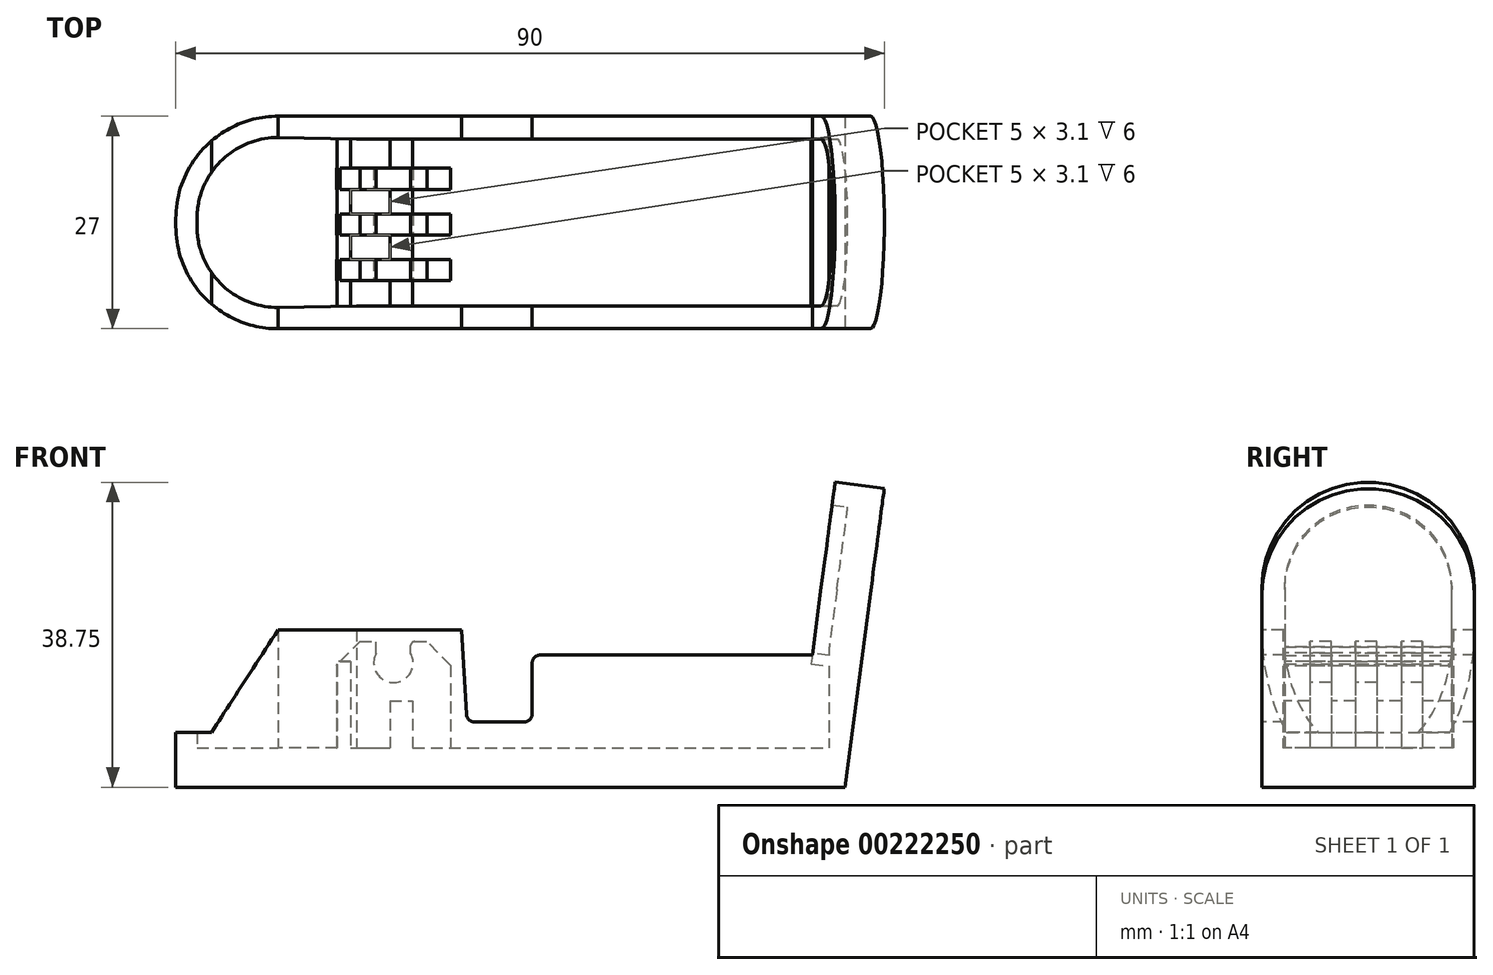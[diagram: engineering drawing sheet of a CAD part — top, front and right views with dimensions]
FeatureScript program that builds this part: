
annotation { "Feature Type Name" : "Feature", "Feature Type Description" : "" }
export const myFeature = defineFeature(function(context is Context, id is Id, definition is map)
    precondition{}
    {
        {
            var Q0;
            Q0=qCreatedBy(makeId("Top.planeOp"),FACE);
            var sketch = newSketch(context, id + "F0", { "sketchPlane" : qUnion([Q0])});
            skLineSegment(sketch, "E0.bottom", {"start": v(-17.1, 7) * mm, "end": v(54.9, 7) * mm});
            skLineSegment(sketch, "E0.top", {"start": v(-17.1, -20) * mm, "end": v(54.9, -20) * mm});
            skLineSegment(sketch, "E0.left", {"start": v(-30.1, -6) * mm, "end": v(-30.1, -7) * mm});
            skLineSegment(sketch, "E0.right", {"start": v(54.9, 7) * mm, "end": v(54.9, -20) * mm});
            skPoint(sketch, "E1.visualSharp", {"position": v(-30.1, 7) * mm});
            skArc(sketch, "E1.filletArc", {"start": v(-17.1, 7) * mm, "mid": v(-26.3, 3.19) * mm, "end": v(-30.1, -6) * mm});
            skPoint(sketch, "E2.visualSharp", {"position": v(-30.1, -20) * mm});
            skArc(sketch, "E2.filletArc", {"start": v(-30.1, -7) * mm, "mid": v(-26.3, -16.2) * mm, "end": v(-17.1, -20) * mm});
            skLineSegment(sketch, "E3.2", {"start": v(-7.15, -17.1) * mm, "end": v(52, -17.1) * mm});
            skLineSegment(sketch, "E3.3", {"start": v(-7.15, 4.1) * mm, "end": v(52.9, 4.1) * mm});
            skLineSegment(sketch, "E4", {"start": v(52.9, 7) * mm, "end": v(52.9, -20) * mm});
            skLineSegment(sketch, "E5", {"start": v(52, -17.1) * mm, "end": v(52.9, -17.1) * mm});
            skArc(sketch, "E6.0", {"start": v(-27.4, -7) * mm, "mid": v(-24.39, -14.3) * mm, "end": v(-17.1, -17.3) * mm});
            skLineSegment(sketch, "E6.1", {"start": v(-27.4, -6) * mm, "end": v(-27.4, -7) * mm});
            skArc(sketch, "E6.2", {"start": v(-17.1, 4.3) * mm, "mid": v(-24.39, 1.28) * mm, "end": v(-27.4, -6) * mm});
            skLineSegment(sketch, "E7", {"start": v(-17.1, 4.3) * mm, "end": v(-7.15, 4.1) * mm});
            skLineSegment(sketch, "E8", {"start": v(-7.15, -17.1) * mm, "end": v(-17.1, -17.3) * mm});
            skSolve(sketch);
        }
        {
            var Q0;
            Q0=makeQuery(id+"F0.imprint","IMPRINT",FACE,{"disambiguationData":[TD([[makeQuery(id+"F0.imprint","IMPRINT",EDGE,{"derivedFrom":sQuery(id+"F0.wireOp",EDGE,"E0.bottom")}),-1.0]])]});
            var Q1;
            Q1=makeQuery(id+"F0.imprint","IMPRINT",FACE,{"disambiguationData":[TD([[makeQuery(id+"F0.imprint","IMPRINT",EDGE,{"derivedFrom":sQuery(id+"F0.wireOp",EDGE,"E0.left")}),1.0]])]});
            extrude(context, id + "F1", {"entities" : qUnion([Q0, Q1]), "depth" : 20 * mm});
        }
        {
            var Q0;
            Q0=makeQuery(id+"F0.imprint","IMPRINT",FACE,{"disambiguationData":[TD([[makeQuery(id+"F0.imprint","IMPRINT",EDGE,{"derivedFrom":sQuery(id+"F0.wireOp",EDGE,"E3.2")}),1.0]])]});
            extrude(context, id + "F2", {"entities" : qUnion([Q0]), "operationType" : NewBodyOperationType.ADD, "depth" : 5 * mm});
        }
        {
            var Q0;
            Q0=makeQuery(id+"F1.opExtrude","SWEPT_FACE",FACE,{"disambiguationData":[OSD([sQuery(id+"F0.wireOp",EDGE,"E0.top")])]});
            var sketch = newSketch(context, id + "F3", { "sketchPlane" : qUnion([Q0])});
            skLineSegment(sketch, "E9", {"start": v(-30.1, 0) * mm, "end": v(-17.1, 20) * mm});
            skLineSegment(sketch, "E10", {"start": v(-17.1, 20) * mm, "end": v(-30.11, 20) * mm});
            skLineSegment(sketch, "E11", {"start": v(-30.11, 20) * mm, "end": v(-30.1, 0) * mm});
            skLineSegment(sketch, "E12", {"start": v(-30.1, 0) * mm, "end": v(-30.1, 7) * mm});
            skLineSegment(sketch, "E13", {"start": v(-30.1, 7) * mm, "end": v(-25.56, 7) * mm});
            skSolve(sketch);
        }
        {
            var Q0;
            {var subQ0=sQuery(id+"F3.wireOp",EDGE,"E10");Q0=makeQuery(id+"F3.imprint","IMPRINT",FACE,{"disambiguationData":[TD([[makeQuery(id+"F3.imprint","IMPRINT",EDGE,{"derivedFrom":subQ0}),1.0]])]});}
            extrude(context, id + "F4", {"entities" : qUnion([Q0]), "operationType" : NewBodyOperationType.REMOVE, "oppositeDirection" : true, "depth" : 29.7 * mm});
        }
        {
            var Q0;
            Q0=makeQuery(id+"F1.opExtrude","SWEPT_FACE",FACE,{"disambiguationData":[OSD([sQuery(id+"F0.wireOp",EDGE,"E0.top")])]});
            var sketch = newSketch(context, id + "F5", { "sketchPlane" : qUnion([Q0])});
            skLineSegment(sketch, "E14", {"start": v(54.9, 0) * mm, "end": v(59.9, 37.93) * mm});
            skLineSegment(sketch, "E15", {"start": v(59.9, 37.93) * mm, "end": v(55.63, 38.5) * mm});
            skLineSegment(sketch, "E16", {"start": v(55.63, 38.5) * mm, "end": v(53.1, 19.35) * mm});
            skLineSegment(sketch, "E17", {"start": v(53.1, 19.35) * mm, "end": v(54.9, 0) * mm});
            skSolve(sketch);
        }
        {
            var Q0;
            Q0 = qSketchRegion(id + "F5", true);
            extrude(context, id + "F6", {"entities" : qUnion([Q0]), "operationType" : NewBodyOperationType.ADD, "oppositeDirection" : true, "depth" : 27 * mm});
        }
        {
            var Q0;
            Q0=makeQuery(id+"F6.opExtrude","SWEPT_FACE",FACE,{"disambiguationData":[OSD([sQuery(id+"F5.wireOp",EDGE,"E16")])]});
            var sketch = newSketch(context, id + "F7", { "sketchPlane" : qUnion([Q0])});
            skLineSegment(sketch, "E18", {"start": v(-7, 26.78) * mm, "end": v(-7, 31.93) * mm});
            skLineSegment(sketch, "E19", {"start": v(6.5, 45.43) * mm, "end": v(6.5, 45.43) * mm});
            skLineSegment(sketch, "E20", {"start": v(20, 31.93) * mm, "end": v(20, 26.78) * mm});
            skLineSegment(sketch, "E21", {"start": v(20, 26.78) * mm, "end": v(-7, 26.78) * mm});
            skPoint(sketch, "E22.visualSharp", {"position": v(-7, 45.43) * mm});
            skArc(sketch, "E22.filletArc", {"start": v(6.5, 45.43) * mm, "mid": v(-3.04, 41.48) * mm, "end": v(-7, 31.93) * mm});
            skPoint(sketch, "E23.visualSharp", {"position": v(20, 45.43) * mm});
            skArc(sketch, "E23.filletArc", {"start": v(20, 31.93) * mm, "mid": v(16.05, 41.48) * mm, "end": v(6.5, 45.43) * mm});
            skLineSegment(sketch, "E24.0", {"start": v(-4.1, 26.78) * mm, "end": v(-4.1, 31.93) * mm});
            skArc(sketch, "E24.1", {"start": v(6.5, 42.53) * mm, "mid": v(-0.99, 39.43) * mm, "end": v(-4.1, 31.93) * mm});
            skArc(sketch, "E24.2", {"start": v(17.1, 31.93) * mm, "mid": v(14, 39.43) * mm, "end": v(6.5, 42.53) * mm});
            skLineSegment(sketch, "E24.3", {"start": v(17.1, 31.93) * mm, "end": v(17.1, 26.78) * mm});
            skLineSegment(sketch, "E25", {"start": v(-4.48, 23.53) * mm, "end": v(17.41, 23.53) * mm});
            skLineSegment(sketch, "E26", {"start": v(17.41, 23.53) * mm, "end": v(17.41, 22.17) * mm});
            skLineSegment(sketch, "E27", {"start": v(17.41, 22.17) * mm, "end": v(-4.48, 22.17) * mm});
            skLineSegment(sketch, "E28", {"start": v(-4.48, 22.17) * mm, "end": v(-4.48, 23.53) * mm});
            skSolve(sketch);
        }
        {
            var Q0;
            {var subQ0=sQuery(id+"F7.wireOp",EDGE,"E22.filletArc");Q0=makeQuery(id+"F7.imprint","IMPRINT",FACE,{"disambiguationData":[TD([[makeQuery(id+"F7.imprint","IMPRINT",EDGE,{"derivedFrom":subQ0}),-1.0]])]});}
            var Q1;
            {var subQ0=sQuery(id+"F7.wireOp",EDGE,"E23.filletArc");Q1=makeQuery(id+"F7.imprint","IMPRINT",FACE,{"disambiguationData":[TD([[makeQuery(id+"F7.imprint","IMPRINT",EDGE,{"derivedFrom":subQ0}),-1.0]])]});}
            extrude(context, id + "F8", {"entities" : qUnion([Q0, Q1]), "operationType" : NewBodyOperationType.REMOVE, "oppositeDirection" : true, "depth" : 25 * mm});
        }
        {
            var Q0;
            {var subQ3=sQuery(id+"F7.wireOp",EDGE,"E18");Q0=makeQuery(id+"F7.imprint","IMPRINT",FACE,{"disambiguationData":[TD([[makeQuery(id+"F7.imprint","IMPRINT",EDGE,{"derivedFrom":subQ3}),1.0]])]});}
            extrude(context, id + "F9", {"entities" : qUnion([Q0]), "operationType" : NewBodyOperationType.ADD, "depth" : 2 * mm});
        }
        {
            var Q0;
            {var subQ0=sQuery(id+"F7.wireOp",EDGE,"E21");Q0=makeQuery(id+"F9.opExtrude","SWEPT_FACE",FACE,{"disambiguationData":[OSD([subQ0]),TDD([makeQuery(id+"F7.imprint","IMPRINT",EDGE,{"disambiguationData":[TD([[makeQuery(id+"F7.imprint","INTERSECT",VERTEX,{"derivedFrom":[sQuery(id+"F7.wireOp",EDGE,"E18"),subQ0]}),-1.0]])],"derivedFrom":subQ0})])]});}
            var Q1;
            {var subQ0=sQuery(id+"F7.wireOp",EDGE,"E21");Q1=makeQuery(id+"F9.opExtrude","SWEPT_FACE",FACE,{"disambiguationData":[OSD([subQ0]),TDD([makeQuery(id+"F7.imprint","IMPRINT",EDGE,{"disambiguationData":[TD([[makeQuery(id+"F7.imprint","INTERSECT",VERTEX,{"derivedFrom":[sQuery(id+"F7.wireOp",EDGE,"E20"),subQ0]}),1.0]])],"derivedFrom":subQ0})])]});}
            var Q2;
            Q2=makeQuery(id+"F1.opExtrude","CAP_FACE",FACE,{"disambiguationData":[OSD([sQuery(id+"F0.wireOp",EDGE,"E0.bottom"),sQuery(id+"F0.wireOp",EDGE,"E0.top"),sQuery(id+"F0.wireOp",EDGE,"E0.left"),sQuery(id+"F0.wireOp",EDGE,"E0.right"),sQuery(id+"F0.wireOp",EDGE,"E1.filletArc"),sQuery(id+"F0.wireOp",EDGE,"E2.filletArc"),sQuery(id+"F0.wireOp",EDGE,"E3.0"),sQuery(id+"F0.wireOp",EDGE,"E3.1"),sQuery(id+"F0.wireOp",EDGE,"E3.2"),sQuery(id+"F0.wireOp",EDGE,"E3.3"),sQuery(id+"F0.wireOp",EDGE,"E3.4"),sQuery(id+"F0.wireOp",EDGE,"E3.5")])],"isStart":false});
            extrude(context, id + "F10", {"entities" : qUnion([Q0, Q1]), "operationType" : NewBodyOperationType.ADD, "endBound" : BoundingType.UP_TO_SURFACE, "endBoundEntityFace" : qUnion([Q2]), "depth" : 25 * mm});
        }
        {
            var Q0;
            {var subQ0=sQuery(id+"F7.wireOp",EDGE,"E20");Q0=makeQuery(id+"F10.boolean.opBoolean","MERGE",FACE,{"derivedFrom":[makeQuery(id+"F9.boolean.opBoolean","MERGE",FACE,{"derivedFrom":[makeQuery(id+"F6.boolean.opBoolean","MERGE",FACE,{"derivedFrom":[makeQuery(id+"F1.opExtrude","SWEPT_FACE",FACE,{"disambiguationData":[OSD([sQuery(id+"F0.wireOp",EDGE,"E0.top")])]}),makeQuery(id+"F6.opExtrude","CAP_FACE",FACE,{"disambiguationData":[OSD([sQuery(id+"F5.wireOp",EDGE,"E14"),sQuery(id+"F5.wireOp",EDGE,"E15"),sQuery(id+"F5.wireOp",EDGE,"E16"),sQuery(id+"F5.wireOp",EDGE,"E17")])],"isStart":true})]}),makeQuery(id+"F9.opExtrude","SWEPT_FACE",FACE,{"disambiguationData":[OSD([subQ0])]})]}),makeQuery(id+"F10.opExtrude","SWEPT_FACE",FACE,{"disambiguationData":[OSD([subQ0,sQuery(id+"F7.wireOp",EDGE,"E21")])]})]});}
            var sketch = newSketch(context, id + "F11", { "sketchPlane" : qUnion([Q0])});
            skLineSegment(sketch, "E29", {"start": v(15.18, 16.8) * mm, "end": v(15.18, 20) * mm});
            skLineSegment(sketch, "E30", {"start": v(15.18, 20) * mm, "end": v(51.18, 20) * mm});
            skLineSegment(sketch, "E31", {"start": v(51.18, 20) * mm, "end": v(50.76, 16.8) * mm});
            skLineSegment(sketch, "E32", {"start": v(50.76, 16.8) * mm, "end": v(16.18, 16.8) * mm});
            skLineSegment(sketch, "E33", {"start": v(15.18, 15.8) * mm, "end": v(15.18, 9.3) * mm});
            skLineSegment(sketch, "E34", {"start": v(14.18, 8.3) * mm, "end": v(7.82, 8.3) * mm});
            skLineSegment(sketch, "E35", {"start": v(6.82, 9.24) * mm, "end": v(6.18, 20) * mm});
            skLineSegment(sketch, "E36", {"start": v(6.18, 20) * mm, "end": v(15.18, 20) * mm});
            skPoint(sketch, "E37.visualSharp", {"position": v(6.88, 8.3) * mm});
            skArc(sketch, "E37.filletArc", {"start": v(6.82, 9.24) * mm, "mid": v(7.13, 8.57) * mm, "end": v(7.82, 8.3) * mm});
            skPoint(sketch, "E38.visualSharp", {"position": v(15.18, 8.3) * mm});
            skArc(sketch, "E38.filletArc", {"start": v(14.18, 8.3) * mm, "mid": v(14.88, 8.6) * mm, "end": v(15.18, 9.3) * mm});
            skPoint(sketch, "E39.visualSharp", {"position": v(15.18, 16.8) * mm});
            skArc(sketch, "E39.filletArc", {"start": v(16.18, 16.8) * mm, "mid": v(15.47, 16.5) * mm, "end": v(15.18, 15.8) * mm});
            skSolve(sketch);
        }
        {
            var Q0;
            Q0=makeQuery(id+"F11.imprint","IMPRINT",FACE,{"disambiguationData":[TD([[makeQuery(id+"F11.imprint","IMPRINT",EDGE,{"derivedFrom":sQuery(id+"F11.wireOp",EDGE,"E30")}),-1.0]])]});
            extrude(context, id + "F12", {"entities" : qUnion([Q0]), "operationType" : NewBodyOperationType.REMOVE, "oppositeDirection" : true, "depth" : 29 * mm});
        }
        {
            var Q0;
            Q0=makeQuery(id+"F2.opExtrude","CAP_FACE",FACE,{"disambiguationData":[OSD([sQuery(id+"F0.wireOp",EDGE,"E3.0"),sQuery(id+"F0.wireOp",EDGE,"E3.1"),sQuery(id+"F0.wireOp",EDGE,"E3.2"),sQuery(id+"F0.wireOp",EDGE,"E3.3"),sQuery(id+"F0.wireOp",EDGE,"E3.4"),sQuery(id+"F0.wireOp",EDGE,"E3.5")])],"isStart":false});
            var sketch = newSketch(context, id + "F13", { "sketchPlane" : qUnion([Q0])});
            skLineSegment(sketch, "E40.bottom", {"start": v(-9.7, -5.4) * mm, "end": v(4.8, -5.4) * mm});
            skLineSegment(sketch, "E40.top", {"start": v(-9.7, -8.1) * mm, "end": v(4.8, -8.1) * mm});
            skLineSegment(sketch, "E40.left", {"start": v(-9.7, -5.4) * mm, "end": v(-9.7, -8.1) * mm});
            skLineSegment(sketch, "E40.right", {"start": v(4.8, -5.4) * mm, "end": v(4.8, -8.1) * mm});
            skLineSegment(sketch, "E41.bottom", {"start": v(-9.7, -11.2) * mm, "end": v(4.8, -11.2) * mm});
            skLineSegment(sketch, "E41.top", {"start": v(-9.7, -13.9) * mm, "end": v(4.8, -13.9) * mm});
            skLineSegment(sketch, "E41.left", {"start": v(-9.7, -11.2) * mm, "end": v(-9.7, -13.9) * mm});
            skLineSegment(sketch, "E41.right", {"start": v(4.8, -11.2) * mm, "end": v(4.8, -13.9) * mm});
            skLineSegment(sketch, "E42.0", {"start": v(-9.7, -2.3) * mm, "end": v(4.8, -2.3) * mm});
            skLineSegment(sketch, "E43.0", {"start": v(-9.7, 0.4) * mm, "end": v(4.8, 0.4) * mm});
            skLineSegment(sketch, "E44", {"start": v(-9.7, 0.4) * mm, "end": v(-9.7, -2.3) * mm});
            skLineSegment(sketch, "E45", {"start": v(4.8, -2.3) * mm, "end": v(4.8, 0.4) * mm});
            skLineSegment(sketch, "E46", {"start": v(-2.45, -5.4) * mm, "end": v(-2.45, -8.1) * mm});
            skSolve(sketch);
        }
        {
            var Q0;
            Q0=makeQuery(id+"F13.imprint","IMPRINT",FACE,{"disambiguationData":[TD([[makeQuery(id+"F13.imprint","IMPRINT",EDGE,{"derivedFrom":sQuery(id+"F13.wireOp",EDGE,"E41.bottom")}),-1.0]])]});
            var Q1;
            {var subQ5=sQuery(id+"F13.wireOp",EDGE,"E40.bottom");Q1=makeQuery(id+"F13.imprint","IMPRINT",FACE,{"disambiguationData":[TD([[makeQuery(id+"F13.imprint","IMPRINT",EDGE,{"derivedFrom":subQ5}),-1.0]])]});}
            var Q2;
            {var subQ5=sQuery(id+"F13.wireOp",EDGE,"E40.top");Q2=makeQuery(id+"F13.imprint","IMPRINT",FACE,{"disambiguationData":[TD([[makeQuery(id+"F13.imprint","IMPRINT",EDGE,{"derivedFrom":subQ5}),1.0]])]});}
            var Q3;
            Q3=makeQuery(id+"F13.imprint","IMPRINT",FACE,{"disambiguationData":[TD([[makeQuery(id+"F13.imprint","IMPRINT",EDGE,{"derivedFrom":sQuery(id+"F13.wireOp",EDGE,"E42.0")}),1.0]])]});
            extrude(context, id + "F14", {"entities" : qUnion([Q0, Q1, Q2, Q3]), "operationType" : NewBodyOperationType.ADD, "depth" : 13.5 * mm});
        }
        {
            var Q0;
            Q0=makeQuery(id+"F14.opExtrude","SWEPT_FACE",FACE,{"disambiguationData":[OSD([sQuery(id+"F13.wireOp",EDGE,"E41.top")])]});
            var sketch = newSketch(context, id + "F15", { "sketchPlane" : qUnion([Q0])});
            skCircle(sketch, "E47", {"center": v(-2.45, 15.8) * mm, "radius": 2.5 * mm});
            skLineSegment(sketch, "E48", {"start": v(-2.45, 18.5) * mm, "end": v(-4.65, 18.5) * mm});
            skLineSegment(sketch, "E49", {"start": v(-2.45, 18.5) * mm, "end": v(-0.25, 18.5) * mm});
            skLineSegment(sketch, "E50", {"start": v(-0.25, 18.5) * mm, "end": v(-0.25, 16.99) * mm});
            skLineSegment(sketch, "E51", {"start": v(-4.65, 18.5) * mm, "end": v(-4.65, 16.99) * mm});
            skSolve(sketch);
        }
        {
            var Q0;
            Q0 = qSketchRegion(id + "F15", true);
            extrude(context, id + "F16", {"entities" : qUnion([Q0]), "operationType" : NewBodyOperationType.REMOVE, "oppositeDirection" : true, "depth" : 15 * mm});
        }
        {
            var Q0;
            Q0=makeQuery(id+"F14.opExtrude","CAP_EDGE",EDGE,{"disambiguationData":[OSD([sQuery(id+"F13.wireOp",EDGE,"E45")])],"isStart":false});
            var Q1;
            Q1=makeQuery(id+"F14.opExtrude","CAP_EDGE",EDGE,{"disambiguationData":[OSD([sQuery(id+"F13.wireOp",EDGE,"E40.right")])],"isStart":false});
            var Q2;
            Q2=makeQuery(id+"F14.opExtrude","CAP_EDGE",EDGE,{"disambiguationData":[OSD([sQuery(id+"F13.wireOp",EDGE,"E44")])],"isStart":false});
            var Q3;
            Q3=makeQuery(id+"F14.opExtrude","CAP_EDGE",EDGE,{"disambiguationData":[OSD([sQuery(id+"F13.wireOp",EDGE,"E40.left")])],"isStart":false});
            var Q4;
            Q4=makeQuery(id+"F14.opExtrude","CAP_EDGE",EDGE,{"disambiguationData":[OSD([sQuery(id+"F13.wireOp",EDGE,"E41.left")])],"isStart":false});
            var Q5;
            Q5=makeQuery(id+"F14.opExtrude","CAP_EDGE",EDGE,{"disambiguationData":[OSD([sQuery(id+"F13.wireOp",EDGE,"E41.right")])],"isStart":false});
            chamfer(context, id + "F17", {"entities" : qUnion([Q0, Q1, Q2, Q3, Q4, Q5]), "width" : 3 * mm, "tangentPropagation" : true});
        }
        {
            var Q0;
            Q0=makeQuery(id+"F2.opExtrude","CAP_FACE",FACE,{"disambiguationData":[OSD([sQuery(id+"F0.wireOp",EDGE,"E3.2"),sQuery(id+"F0.wireOp",EDGE,"E3.3"),sQuery(id+"F0.wireOp",EDGE,"E4"),sQuery(id+"F0.wireOp",EDGE,"E5"),sQuery(id+"F0.wireOp",EDGE,"E6.0"),sQuery(id+"F0.wireOp",EDGE,"E6.1"),sQuery(id+"F0.wireOp",EDGE,"E6.2"),sQuery(id+"F0.wireOp",EDGE,"E7"),sQuery(id+"F0.wireOp",EDGE,"E8")])],"isStart":false});
            var sketch = newSketch(context, id + "F18", { "sketchPlane" : qUnion([Q0])});
            skLineSegment(sketch, "E52.bottom", {"start": v(-9.6, 5.13) * mm, "end": v(-7.9, 5.13) * mm});
            skLineSegment(sketch, "E52.top", {"start": v(-9.6, -18.4) * mm, "end": v(-7.9, -18.4) * mm});
            skLineSegment(sketch, "E52.left", {"start": v(-9.6, 5.13) * mm, "end": v(-9.6, -18.4) * mm});
            skLineSegment(sketch, "E52.right", {"start": v(-7.9, 5.13) * mm, "end": v(-7.9, -18.4) * mm});
            skLineSegment(sketch, "E53.bottom", {"start": v(-2.9, 4.75) * mm, "end": v(0, 4.75) * mm});
            skLineSegment(sketch, "E53.top", {"start": v(-2.9, -17.95) * mm, "end": v(0, -17.95) * mm});
            skLineSegment(sketch, "E53.left", {"start": v(-2.9, 4.75) * mm, "end": v(-2.9, -17.95) * mm});
            skLineSegment(sketch, "E53.right", {"start": v(0, 4.75) * mm, "end": v(0, -17.95) * mm});
            skSolve(sketch);
        }
        {
            var Q0;
            {var subQ0=sQuery(id+"F18.wireOp",EDGE,"E52.left");var subQ1=makeQuery(id+"F2.opExtrude","CAP_EDGE",EDGE,{"disambiguationData":[OSD([sQuery(id+"F0.wireOp",EDGE,"E7")])],"isStart":false});var subQ2=makeQuery(id+"F18.imprint","INTERSECT",VERTEX,{"derivedFrom":[subQ1,subQ0]});Q0=makeQuery(id+"F18.imprint","IMPRINT",FACE,{"disambiguationData":[TD([[makeQuery(id+"F18.imprint","IMPRINT",EDGE,{"disambiguationData":[TD([[subQ2,-1.0]])],"derivedFrom":subQ0}),1.0]])]});}
            var Q1;
            {var subQ0=sQuery(id+"F18.wireOp",EDGE,"E52.left");var subQ1=makeQuery(id+"F14.opExtrude","CAP_EDGE",EDGE,{"disambiguationData":[OSD([sQuery(id+"F13.wireOp",EDGE,"E42.0")])],"isStart":true});var subQ2=makeQuery(id+"F18.imprint","INTERSECT",VERTEX,{"derivedFrom":[subQ1,subQ0]});Q1=makeQuery(id+"F18.imprint","IMPRINT",FACE,{"disambiguationData":[TD([[makeQuery(id+"F18.imprint","IMPRINT",EDGE,{"disambiguationData":[TD([[subQ2,-1.0]])],"derivedFrom":subQ0}),1.0]])]});}
            var Q2;
            {var subQ0=sQuery(id+"F18.wireOp",EDGE,"E52.left");var subQ1=makeQuery(id+"F14.opExtrude","CAP_EDGE",EDGE,{"disambiguationData":[OSD([sQuery(id+"F13.wireOp",EDGE,"E40.top")])],"isStart":true});var subQ2=makeQuery(id+"F18.imprint","INTERSECT",VERTEX,{"derivedFrom":[subQ1,subQ0]});Q2=makeQuery(id+"F18.imprint","IMPRINT",FACE,{"disambiguationData":[TD([[makeQuery(id+"F18.imprint","IMPRINT",EDGE,{"disambiguationData":[TD([[subQ2,-1.0]])],"derivedFrom":subQ0}),1.0]])]});}
            var Q3;
            {var subQ0=sQuery(id+"F18.wireOp",EDGE,"E52.left");var subQ1=makeQuery(id+"F2.opExtrude","CAP_EDGE",EDGE,{"disambiguationData":[OSD([sQuery(id+"F0.wireOp",EDGE,"E8")])],"isStart":false});var subQ2=makeQuery(id+"F18.imprint","INTERSECT",VERTEX,{"derivedFrom":[subQ1,subQ0]});Q3=makeQuery(id+"F18.imprint","IMPRINT",FACE,{"disambiguationData":[TD([[makeQuery(id+"F18.imprint","IMPRINT",EDGE,{"disambiguationData":[TD([[subQ2,1.0]])],"derivedFrom":subQ0}),1.0]])]});}
            extrude(context, id + "F19", {"entities" : qUnion([Q0, Q1, Q2, Q3]), "operationType" : NewBodyOperationType.ADD, "depth" : 11 * mm});
        }
        {
            var Q0;
            {var subQ0=sQuery(id+"F13.wireOp",EDGE,"E42.0");var subQ2=sQuery(id+"F15.wireOp",EDGE,"E51");Q0=makeQuery(id+"F16.boolean.opBoolean","COPY",EDGE,{"disambiguationData":[TD([makeQuery(id+"F14.opExtrude","SWEPT_FACE",FACE,{"disambiguationData":[OSD([subQ0])]})])],"derivedFrom":makeQuery(id+"F16.opExtrude","SWEPT_EDGE",EDGE,{"disambiguationData":[OSD([sQuery(id+"F13.wireOp",EDGE,"E41.top"),sQuery(id+"F15.wireOp",EDGE,"E48"),subQ2])]})});}
            var Q1;
            {var subQ0=sQuery(id+"F13.wireOp",EDGE,"E42.0");var subQ2=sQuery(id+"F15.wireOp",EDGE,"E50");Q1=makeQuery(id+"F16.boolean.opBoolean","COPY",EDGE,{"disambiguationData":[TD([makeQuery(id+"F14.opExtrude","SWEPT_FACE",FACE,{"disambiguationData":[OSD([subQ0])]})])],"derivedFrom":makeQuery(id+"F16.opExtrude","SWEPT_EDGE",EDGE,{"disambiguationData":[OSD([sQuery(id+"F13.wireOp",EDGE,"E41.top"),sQuery(id+"F15.wireOp",EDGE,"E49"),subQ2])]})});}
            var Q2;
            {var subQ0=sQuery(id+"F13.wireOp",EDGE,"E40.bottom");var subQ2=sQuery(id+"F15.wireOp",EDGE,"E51");Q2=makeQuery(id+"F16.boolean.opBoolean","COPY",EDGE,{"disambiguationData":[TD([makeQuery(id+"F14.opExtrude","SWEPT_FACE",FACE,{"disambiguationData":[OSD([subQ0])]})])],"derivedFrom":makeQuery(id+"F16.opExtrude","SWEPT_EDGE",EDGE,{"disambiguationData":[OSD([sQuery(id+"F13.wireOp",EDGE,"E41.top"),sQuery(id+"F15.wireOp",EDGE,"E48"),subQ2])]})});}
            var Q3;
            {var subQ0=sQuery(id+"F13.wireOp",EDGE,"E40.bottom");var subQ2=sQuery(id+"F15.wireOp",EDGE,"E50");Q3=makeQuery(id+"F16.boolean.opBoolean","COPY",EDGE,{"disambiguationData":[TD([makeQuery(id+"F14.opExtrude","SWEPT_FACE",FACE,{"disambiguationData":[OSD([subQ0])]})])],"derivedFrom":makeQuery(id+"F16.opExtrude","SWEPT_EDGE",EDGE,{"disambiguationData":[OSD([sQuery(id+"F13.wireOp",EDGE,"E41.top"),sQuery(id+"F15.wireOp",EDGE,"E49"),subQ2])]})});}
            var Q4;
            {var subQ0=sQuery(id+"F13.wireOp",EDGE,"E41.bottom");var subQ1=sQuery(id+"F13.wireOp",EDGE,"E41.top");var subQ2=sQuery(id+"F15.wireOp",EDGE,"E51");Q4=makeQuery(id+"F16.boolean.opBoolean","COPY",EDGE,{"disambiguationData":[TD([makeQuery(id+"F14.opExtrude","SWEPT_FACE",FACE,{"disambiguationData":[OSD([subQ0])]})])],"derivedFrom":makeQuery(id+"F16.opExtrude","SWEPT_EDGE",EDGE,{"disambiguationData":[OSD([subQ1,sQuery(id+"F15.wireOp",EDGE,"E48"),subQ2])]})});}
            var Q5;
            {var subQ0=sQuery(id+"F13.wireOp",EDGE,"E41.bottom");var subQ1=sQuery(id+"F13.wireOp",EDGE,"E41.top");var subQ2=sQuery(id+"F15.wireOp",EDGE,"E50");Q5=makeQuery(id+"F16.boolean.opBoolean","COPY",EDGE,{"disambiguationData":[TD([makeQuery(id+"F14.opExtrude","SWEPT_FACE",FACE,{"disambiguationData":[OSD([subQ0])]})])],"derivedFrom":makeQuery(id+"F16.opExtrude","SWEPT_EDGE",EDGE,{"disambiguationData":[OSD([subQ1,sQuery(id+"F15.wireOp",EDGE,"E49"),subQ2])]})});}
            fillet(context, id + "F20", {"entities" : qUnion([Q0, Q1, Q2, Q3, Q4, Q5]), "radius" : 0.5 * mm, "tangentPropagation" : true, "allowEdgeOverflow" : false});
        }
        {
            var Q0;
            {var subQ0=sQuery(id+"F18.wireOp",EDGE,"E53.left");var subQ1=makeQuery(id+"F2.opExtrude","CAP_EDGE",EDGE,{"disambiguationData":[OSD([sQuery(id+"F0.wireOp",EDGE,"E3.3")])],"isStart":false});var subQ2=makeQuery(id+"F18.imprint","INTERSECT",VERTEX,{"derivedFrom":[subQ1,subQ0]});Q0=makeQuery(id+"F18.imprint","IMPRINT",FACE,{"disambiguationData":[TD([[makeQuery(id+"F18.imprint","IMPRINT",EDGE,{"disambiguationData":[TD([[subQ2,-1.0]])],"derivedFrom":subQ0}),1.0]])]});}
            var Q1;
            {var subQ0=sQuery(id+"F18.wireOp",EDGE,"E53.left");var subQ1=makeQuery(id+"F14.opExtrude","CAP_EDGE",EDGE,{"disambiguationData":[OSD([sQuery(id+"F13.wireOp",EDGE,"E42.0")])],"isStart":true});var subQ2=makeQuery(id+"F18.imprint","INTERSECT",VERTEX,{"derivedFrom":[subQ1,subQ0]});Q1=makeQuery(id+"F18.imprint","IMPRINT",FACE,{"disambiguationData":[TD([[makeQuery(id+"F18.imprint","IMPRINT",EDGE,{"disambiguationData":[TD([[subQ2,-1.0]])],"derivedFrom":subQ0}),1.0]])]});}
            var Q2;
            {var subQ0=sQuery(id+"F18.wireOp",EDGE,"E53.left");var subQ1=makeQuery(id+"F14.opExtrude","CAP_EDGE",EDGE,{"disambiguationData":[OSD([sQuery(id+"F13.wireOp",EDGE,"E40.top")])],"isStart":true});var subQ2=makeQuery(id+"F18.imprint","INTERSECT",VERTEX,{"derivedFrom":[subQ1,subQ0]});Q2=makeQuery(id+"F18.imprint","IMPRINT",FACE,{"disambiguationData":[TD([[makeQuery(id+"F18.imprint","IMPRINT",EDGE,{"disambiguationData":[TD([[subQ2,-1.0]])],"derivedFrom":subQ0}),1.0]])]});}
            var Q3;
            {var subQ0=sQuery(id+"F18.wireOp",EDGE,"E53.left");var subQ3=makeQuery(id+"F14.opExtrude","CAP_EDGE",EDGE,{"disambiguationData":[OSD([sQuery(id+"F13.wireOp",EDGE,"E41.top")])],"isStart":true});var subQ4=makeQuery(id+"F18.imprint","INTERSECT",VERTEX,{"derivedFrom":[subQ3,subQ0]});Q3=makeQuery(id+"F18.imprint","IMPRINT",FACE,{"disambiguationData":[TD([[makeQuery(id+"F18.imprint","IMPRINT",EDGE,{"disambiguationData":[TD([[subQ4,-1.0]])],"derivedFrom":subQ3}),-1.0]])]});}
            extrude(context, id + "F21", {"entities" : qUnion([Q0, Q1, Q2, Q3]), "operationType" : NewBodyOperationType.ADD, "depth" : 6 * mm});
        }
        {
            var Q0;
            Q0=makeQuery(id+"F1.opExtrude","CAP_EDGE",EDGE,{"disambiguationData":[OSD([sQuery(id+"F0.wireOp",EDGE,"E4")])],"isStart":false});
            chamfer(context, id + "F22", {"entities" : qUnion([Q0]), "width" : 2.2 * mm, "tangentPropagation" : true});
        }
        {
            var Q0;
            Q0=makeQuery(id+"F7.imprint","IMPRINT",FACE,{"disambiguationData":[TD([[makeQuery(id+"F7.imprint","IMPRINT",EDGE,{"derivedFrom":sQuery(id+"F7.wireOp",EDGE,"E25")}),-1.0]])]});
            extrude(context, id + "F23", {"entities" : qUnion([Q0]), "operationType" : NewBodyOperationType.ADD, "depth" : 2 * mm, "hasSecondDirection" : true, "secondDirectionBound" : SecondDirectionBoundingType.UP_TO_NEXT, "secondDirectionOppositeDirection" : true, "secondDirectionDepth" : 25 * mm});
        }
    });
